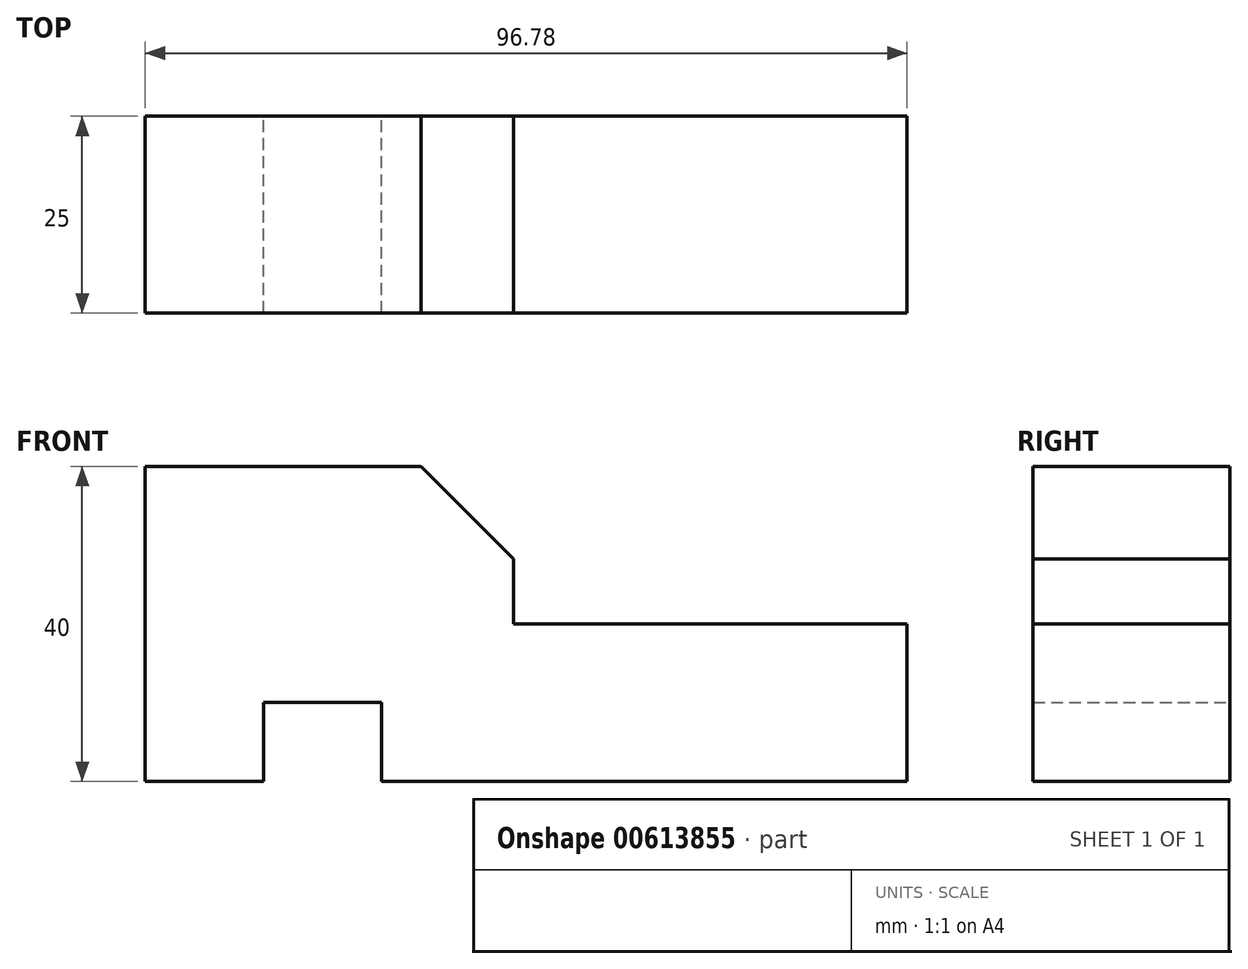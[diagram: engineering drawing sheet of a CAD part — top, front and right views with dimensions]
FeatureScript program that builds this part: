
annotation { "Feature Type Name" : "Feature", "Feature Type Description" : "" }
export const myFeature = defineFeature(function(context is Context, id is Id, definition is map)
    precondition{}
    {
        {
            var Q0;
            Q0=qCreatedBy(makeId("Front.planeOp"),FACE);
            var sketch = newSketch(context, id + "F0", { "sketchPlane" : qUnion([Q0])});
            skLineSegment(sketch, "E0", {"start": v(-70.4, 40) * mm, "end": v(-35.4, 40) * mm});
            skLineSegment(sketch, "E1", {"start": v(-23.63, 28.22) * mm, "end": v(-23.63, 20) * mm});
            skLineSegment(sketch, "E2", {"start": v(-23.63, 20) * mm, "end": v(26.37, 20) * mm});
            skLineSegment(sketch, "E3", {"start": v(26.37, 20) * mm, "end": v(26.37, 0) * mm});
            skLineSegment(sketch, "E4", {"start": v(26.37, 0) * mm, "end": v(-40.4, 0) * mm});
            skLineSegment(sketch, "E5", {"start": v(-40.4, 0) * mm, "end": v(-40.4, 10) * mm});
            skLineSegment(sketch, "E6", {"start": v(-40.4, 10) * mm, "end": v(-55.4, 10) * mm});
            skLineSegment(sketch, "E7", {"start": v(-55.4, 10) * mm, "end": v(-55.4, 0) * mm});
            skLineSegment(sketch, "E8", {"start": v(-55.4, 0) * mm, "end": v(-70.4, 0) * mm});
            skLineSegment(sketch, "E9", {"start": v(-70.4, 0) * mm, "end": v(-70.4, 40) * mm});
            skPoint(sketch, "E10.visualSharp", {"position": v(-23.63, 40) * mm});
            skLineSegment(sketch, "E11", {"start": v(-23.63, 28.22) * mm, "end": v(-35.4, 40) * mm});
            skPoint(sketch, "E12.orphan", {"position": v(-23.63, 36.45) * mm});
            skSolve(sketch);
        }
        {
            var Q0;
            Q0 = qSketchRegion(id + "F0", true);
            extrude(context, id + "F1", {"entities" : qUnion([Q0]), "depth" : 25 * mm, "offsetDistance" : 25 * mm});
        }
    });
